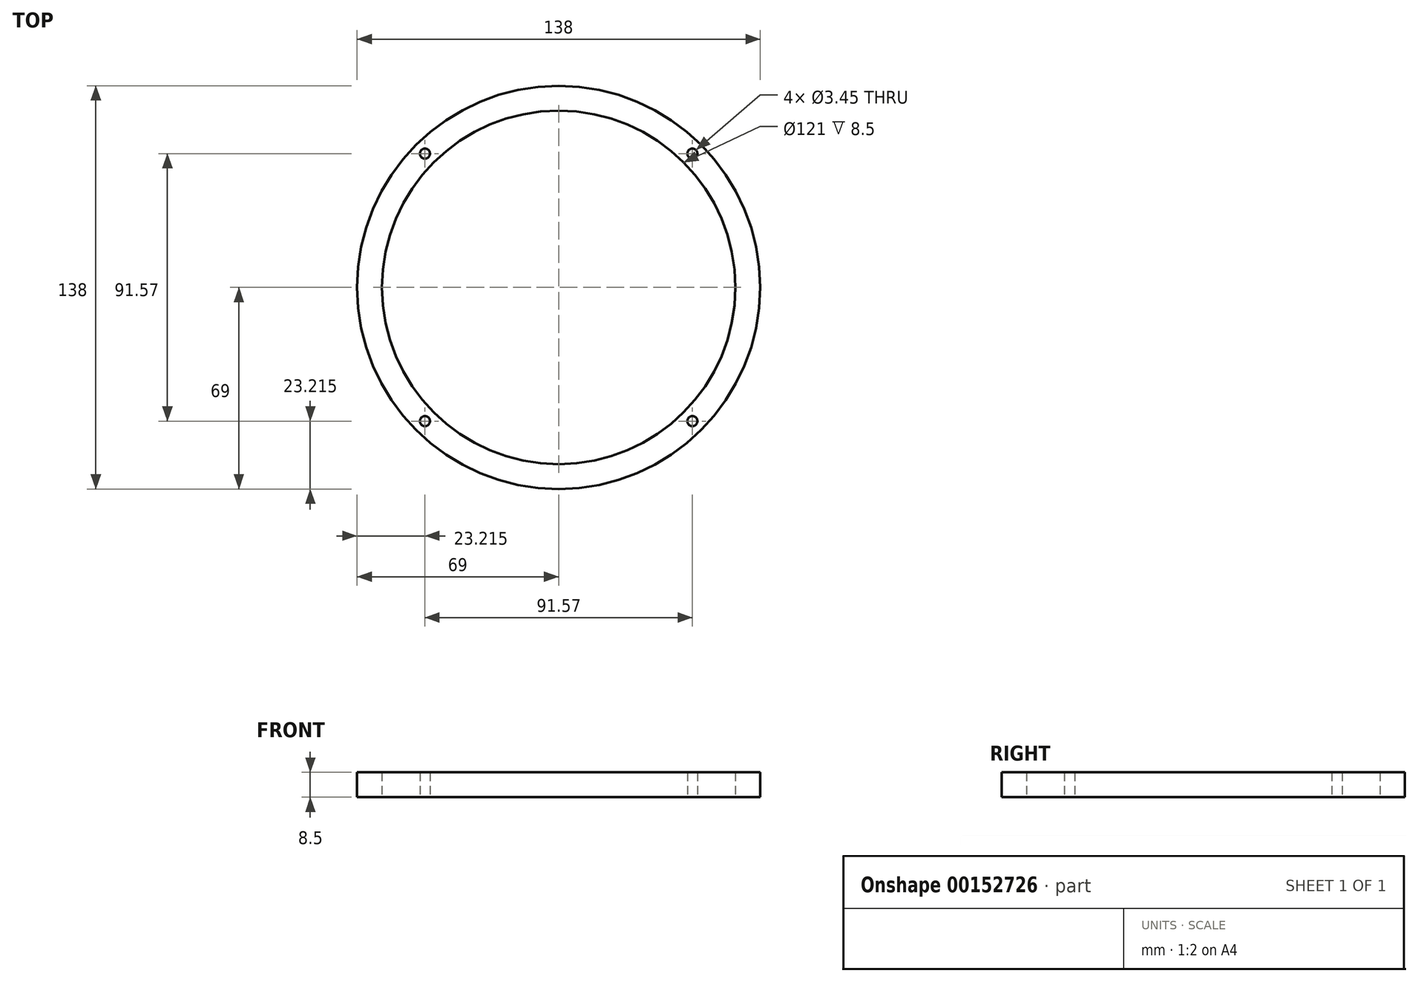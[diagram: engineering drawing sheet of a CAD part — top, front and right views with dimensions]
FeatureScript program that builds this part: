
annotation { "Feature Type Name" : "Feature", "Feature Type Description" : "" }
export const myFeature = defineFeature(function(context is Context, id is Id, definition is map)
    precondition{}
    {
        {
            var Q0;
            Q0=qCreatedBy(makeId("Top.planeOp"),FACE);
            var sketch = newSketch(context, id + "F0", { "sketchPlane" : qUnion([Q0])});
            skCircle(sketch, "E0", {"center": v(0, 0) * mm, "radius": 69 * mm});
            skCircle(sketch, "E1", {"center": v(0, 0) * mm, "radius": 60.5 * mm});
            skCircle(sketch, "E2", {"center": v(-45.79, 45.79) * mm, "radius": 4.25 * mm, "construction": true});
            skLineSegment(sketch, "E3.bottom", {"start": v(-45.79, 45.79) * mm, "end": v(45.79, 45.79) * mm, "construction": true});
            skLineSegment(sketch, "E3.top", {"start": v(-45.79, -45.79) * mm, "end": v(45.79, -45.79) * mm, "construction": true});
            skLineSegment(sketch, "E3.left", {"start": v(-45.79, 45.79) * mm, "end": v(-45.79, -45.79) * mm, "construction": true});
            skLineSegment(sketch, "E3.right", {"start": v(45.79, 45.79) * mm, "end": v(45.79, -45.79) * mm, "construction": true});
            skCircle(sketch, "E4", {"center": v(-45.79, 45.79) * mm, "radius": 1.73 * mm});
            skCircle(sketch, "E5", {"center": v(-45.79, -45.79) * mm, "radius": 1.73 * mm});
            skCircle(sketch, "E6", {"center": v(45.79, -45.79) * mm, "radius": 1.73 * mm});
            skCircle(sketch, "E7", {"center": v(45.79, 45.79) * mm, "radius": 1.73 * mm});
            skSolve(sketch);
        }
        {
            var Q0;
            Q0 = qSketchRegion(id + "F0", true);
            extrude(context, id + "F1", {"entities" : qUnion([Q0]), "depth" : 8.5 * mm});
        }
    });
